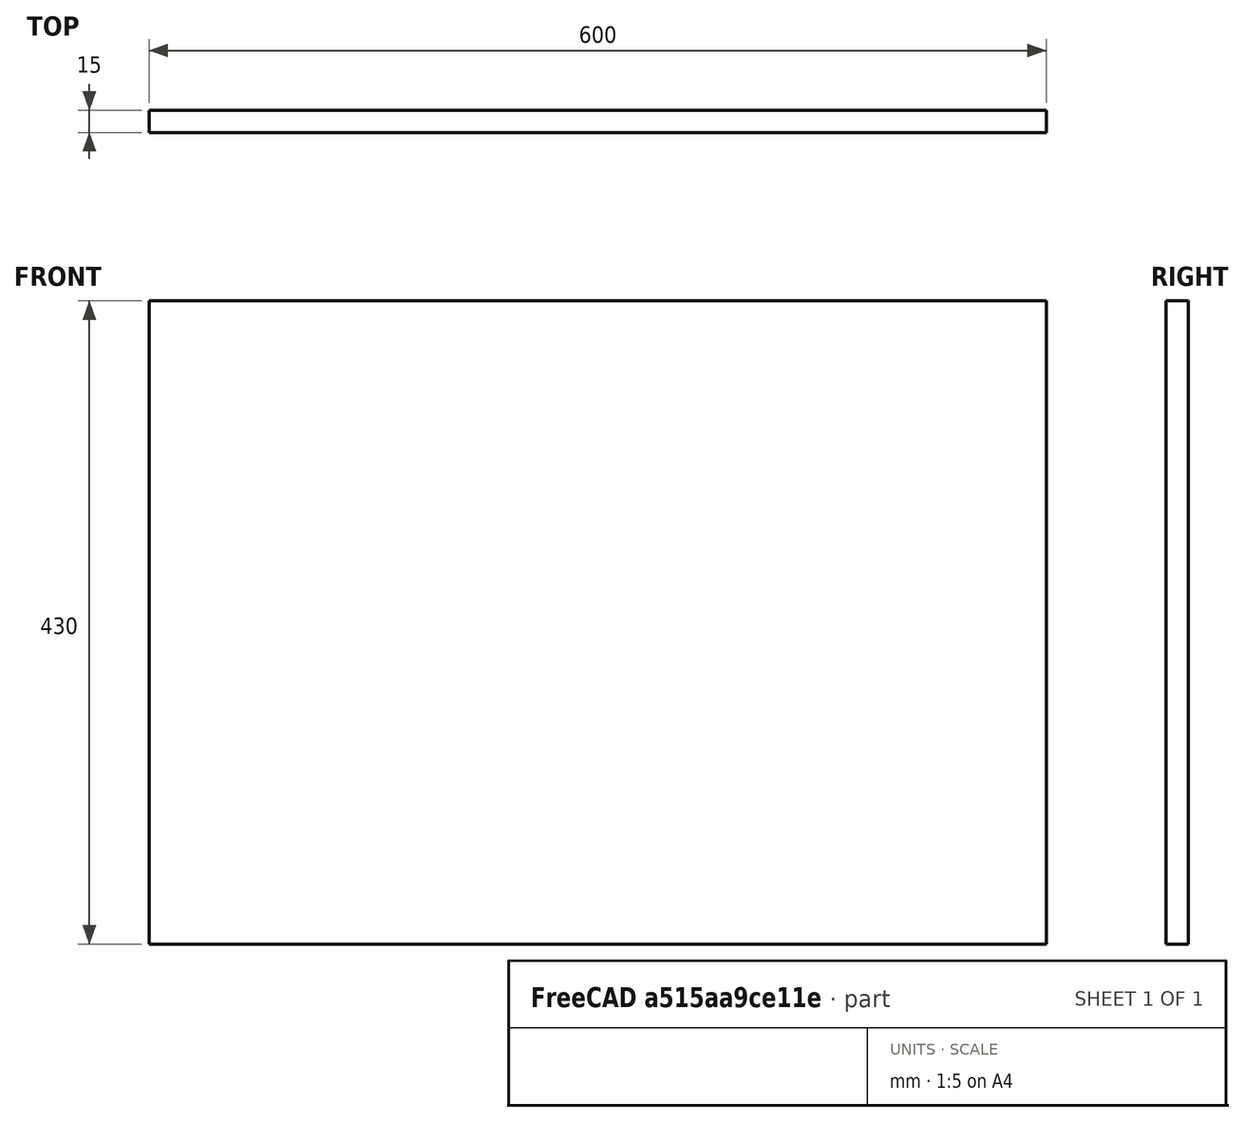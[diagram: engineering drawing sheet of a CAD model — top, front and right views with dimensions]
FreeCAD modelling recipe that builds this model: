
FCSTD DOCUMENT  (FreeCAD 1.0R39319 (Git))
Label: back_bottom_door
License: All rights reserved
LicenseURL: https://en.wikipedia.org/wiki/All_rights_reserved
objects: Sketcher::SketchObject×1, PartDesign::Pad×1, PartDesign::Body×1
note: 6 computed .brp shape members not serialized (recipe doc carries the construction recipe); baked Part::Feature solids carry a one-line shape summary decoded from their .brp

FEATURE [Sketcher::SketchObject] Sketch  label="back_bottom_door_s"
  ArcFitTolerance = 1e-06
  AttachmentSupport = -> [XZ_Plane]
  FullyConstrained = true
  MakeInternals = false
  MapMode = 5
  Placement = pos=(0,0,0) rot=(1,0,0;1.5708rad)
  sketch-geometry (4):
    g0: LineSegment StartX=0 StartY=0 StartZ=0 EndX=600 EndY=0 EndZ=0
    g1: LineSegment StartX=600 StartY=0 StartZ=0 EndX=600 EndY=430 EndZ=0
    g2: LineSegment StartX=600 StartY=430 StartZ=0 EndX=0 EndY=430 EndZ=0
    g3: LineSegment StartX=0 StartY=430 StartZ=0 EndX=0 EndY=0 EndZ=0
  constraints (11):
    c: Coincident(g0,g1)
    c: Coincident(g1,g2)
    c: Coincident(g2,g3)
    c: Coincident(g3,g0)
    c: Horizontal(g0)
    c: Horizontal(g2)
    c: Vertical(g1)
    c: Vertical(g3)
    c: Coincident(g0,g-1)
    c: DistanceX(g2,g2) = 600
    c: DistanceY(g3,g3) = 430
FEATURE [PartDesign::Pad] Pad  label="back_bottom_door"
  Direction = (0,-1,2e-16)
  Length = 15
  Length2 = 10
  Placement = pos=(0,0,0) rot=(1,0,0;1.5708rad)
  Profile = -> Sketch
  ReferenceAxis = -> Sketch [N_Axis]
  Refine = true
  Suppressed = false
  Type = 0
FEATURE [PartDesign::Body] Body  label="back_bottom_door_body"
  AllowCompound = false
  Group = -> [Sketch,Pad]
  Origin = -> Origin
  Tip = -> Pad
